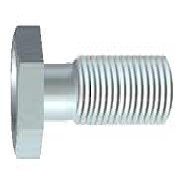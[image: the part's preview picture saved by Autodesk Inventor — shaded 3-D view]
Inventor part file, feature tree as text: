
AUTODESK INVENTOR PART (.ipt)
format: ipt  version: 2017 (Build 210142000, 142)  size: 178,176 bytes
history: native  units: mm (DEFAULTED — no unit token found)
features: sketch x4, extrude x2, chamfer x1, plane x1
ambient origin geometry x7: Origin, YZ Plane, XZ Plane, X Axis, Y Axis, Z Axis, Center Point
bodies: Solid1 (feature_tree), Body (feature_tree)
feature tree (8):
  extrude  "Head"  TaperAngle=90.0deg  [1 undecoded]
  extrude  "Indent"  TaperAngle=0.0deg  [1 undecoded]
  chamfer  "Chamfer1"  Distance=0.39751mm
  plane  "Work Plane1"
  sketch  "Sketch1"  dims[d1=4.1656mm d12=90.0deg]
  sketch  "Sketch2"  dims[d2=2.794mm d3=0.0mm]
  sketch  "Sketch4"  dims[d21=90.0deg d5=0.39751mm d6=0.39761mm d7=0.0mm d8=7.9248mm d9=26.9875mm d10=0.0mm d13=31.75mm d17=7.9248mm d18=6.33984mm d19=0.2804mm d20=0.0mm d77=45.0deg d80=0.0mm d81=0.0mm]
  sketch  "Sketch3"  dims[d4=30.0deg]
note: 2 required parameter values undecoded (feature->parameter linkage not recoverable at this tier; creation-order binding heuristic only, values carry confidence <= 0.55)
